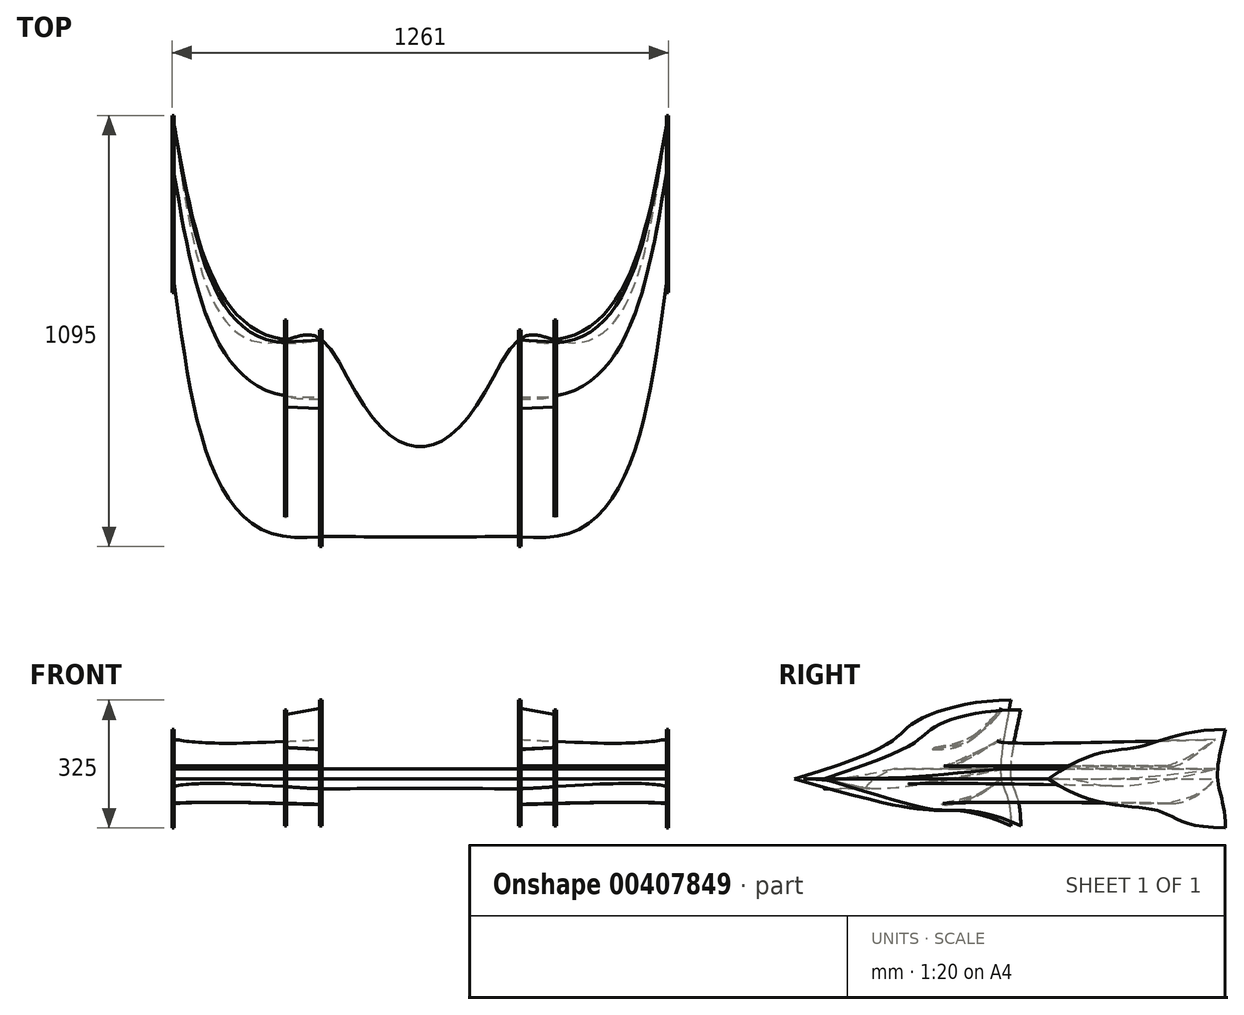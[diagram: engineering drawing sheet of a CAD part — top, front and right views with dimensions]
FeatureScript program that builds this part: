
annotation { "Feature Type Name" : "Feature", "Feature Type Description" : "" }
export const myFeature = defineFeature(function(context is Context, id is Id, definition is map)
    precondition{}
    {
        {
            var Q0;
            Q0=qCreatedBy(makeId("Right.planeOp"),FACE);
            cPlane(context, id + "F0", {"entities" : qUnion([Q0]), "cplaneType" : CPlaneType.OFFSET, "offset" : 250 * mm, "width" : 152.4 * mm, "height" : 152.4 * mm});
        }
        {
            var Q0;
            Q0=qCreatedBy(makeId("Right.planeOp"),FACE);
            cPlane(context, id + "F1", {"entities" : qUnion([Q0]), "cplaneType" : CPlaneType.OFFSET, "offset" : 340 * mm, "width" : 150 * mm, "height" : 150 * mm});
        }
        {
            var Q0;
            Q0=qCreatedBy(makeId("Right.planeOp"),FACE);
            cPlane(context, id + "F2", {"entities" : qUnion([Q0]), "cplaneType" : CPlaneType.OFFSET, "offset" : 625 * mm, "width" : 150 * mm, "height" : 150 * mm});
        }
        {
            var Q0;
            Q0=qCreatedBy(id+"F0.planeOp",FACE);
            var sketch = newSketch(context, id + "F3", { "sketchPlane" : qUnion([Q0])});
            skPoint(sketch, "E0.middle", {"position": v(0, 0) * mm});
            skFitSpline(sketch, "E1", {"points": [v(-275, 0) * mm, v(25, 140) * mm, v(275, 200) * mm], "startDerivative": vector(1552.03, 451.5) * mm, "endDerivative": vector(720.48, 0) * mm});
            skFitSpline(sketch, "E2", {"points": [v(275, 200) * mm, v(250, 0) * mm, v(275, -120) * mm], "startDerivative": vector(-73.02, -379.03) * mm, "endDerivative": vector(0, -547.76) * mm});
            skFitSpline(sketch, "E3", {"points": [v(-275, 0) * mm, v(100, -80) * mm, v(275, -120) * mm], "startDerivative": vector(1389.49, -404.21) * mm, "endDerivative": vector(646.14, -295.38) * mm});
            skSolve(sketch);
        }
        {
            var Q0;
            Q0=qCreatedBy(id+"F1.planeOp",FACE);
            var sketch = newSketch(context, id + "F4", { "sketchPlane" : qUnion([Q0])});
            skFitSpline(sketch, "E4", {"points": [v(-200, 0) * mm, v(75, 127.5) * mm, v(300, 175) * mm], "startDerivative": vector(1403.25, 449.04) * mm, "endDerivative": vector(773.32, 0) * mm});
            skFitSpline(sketch, "E5", {"points": [v(300, 175) * mm, v(275, 0) * mm, v(300, -120) * mm], "startDerivative": vector(-73.33, -336.17) * mm, "endDerivative": vector(0, -528.22) * mm});
            skFitSpline(sketch, "E6", {"points": [v(-200, 0) * mm, v(125, -80) * mm, v(300, -120) * mm], "startDerivative": vector(1299.26, -415.76) * mm, "endDerivative": vector(620.93, -283.86) * mm});
            skSolve(sketch);
        }
        {
            var Q0;
            Q0=qCreatedBy(id+"F2.planeOp",FACE);
            var sketch = newSketch(context, id + "F5", { "sketchPlane" : qUnion([Q0])});
            skFitSpline(sketch, "E7", {"points": [v(370, 0) * mm, v(595, 80) * mm, v(820, 125) * mm], "startDerivative": vector(668.33, 475.26) * mm, "endDerivative": vector(681.8, 0) * mm});
            skFitSpline(sketch, "E8", {"points": [v(820, 125) * mm, v(800, 0) * mm, v(820, -125) * mm], "startDerivative": vector(-60, -250) * mm, "endDerivative": vector(0, -375) * mm});
            skFitSpline(sketch, "E9", {"points": [v(370, 0) * mm, v(645, -80) * mm, v(820, -125) * mm], "startDerivative": vector(605.58, -430.63) * mm, "endDerivative": vector(762.4, 0) * mm});
            skSolve(sketch);
        }
        {
            var Q0;
            Q0=qCreatedBy(makeId("Right.planeOp"),FACE);
            cPlane(context, id + "F6", {"entities" : qUnion([Q0]), "cplaneType" : CPlaneType.OFFSET, "offset" : 160 * mm, "width" : 150 * mm, "height" : 150 * mm});
        }
        {
            var Q0;
            Q0=qCreatedBy(id+"F6.planeOp",FACE);
            var sketch = newSketch(context, id + "F7", { "sketchPlane" : qUnion([Q0])});
            skFitSpline(sketch, "E10", {"points": [v(-250, 0) * mm, v(-75, -25) * mm, v(110, 25) * mm], "startDerivative": vector(535.81, 0) * mm, "endDerivative": vector(529.32, 147.03) * mm});
            skFitSpline(sketch, "E11", {"points": [v(-250, 0) * mm, v(110, 25) * mm], "startDerivative": vector(540, 0) * mm, "endDerivative": vector(540, 75) * mm});
            skSolve(sketch);
        }
        {
            var Q0;
            Q0=qCreatedBy(makeId("Right.planeOp"),FACE);
            cPlane(context, id + "F8", {"entities" : qUnion([Q0]), "cplaneType" : CPlaneType.OFFSET, "offset" : 250 * mm, "width" : 150 * mm, "height" : 150 * mm});
        }
        {
            var Q0;
            Q0=qCreatedBy(id+"F8.planeOp",FACE);
            var sketch = newSketch(context, id + "F9", { "sketchPlane" : qUnion([Q0])});
            skFitSpline(sketch, "E12", {"points": [v(-250, 0) * mm, v(-75, -25) * mm, v(250, 25) * mm], "startDerivative": vector(620.51, 0) * mm, "endDerivative": vector(649.96, 130) * mm});
            skFitSpline(sketch, "E13", {"points": [v(-250, 0) * mm, v(250, 25) * mm], "startDerivative": vector(750, 0) * mm, "endDerivative": vector(750, 75) * mm});
            skSolve(sketch);
        }
        {
            var Q0;
            Q0=qCreatedBy(id+"F8.planeOp",FACE);
            var sketch = newSketch(context, id + "F10", { "sketchPlane" : qUnion([Q0])});
            skFitSpline(sketch, "E14", {"points": [v(105, 32) * mm, v(125, 32) * mm, v(250, 100) * mm], "startDerivative": vector(59.92, -12.75) * mm, "endDerivative": vector(207.69, 127.5) * mm});
            skFitSpline(sketch, "E15", {"points": [v(105, 32) * mm, v(250, 100) * mm], "startDerivative": vector(153.75, 54) * mm, "endDerivative": vector(281.25, 150) * mm});
            skSolve(sketch);
        }
        {
            var Q0;
            Q0=qCreatedBy(id+"F8.planeOp",FACE);
            var sketch = newSketch(context, id + "F11", { "sketchPlane" : qUnion([Q0])});
            skFitSpline(sketch, "E16", {"points": [v(100, -65) * mm, v(125, -65) * mm, v(250, 0) * mm], "startDerivative": vector(70.52, -13.7) * mm, "endDerivative": vector(266.48, 234.5) * mm});
            skFitSpline(sketch, "E17", {"points": [v(100, -65) * mm, v(250, 0) * mm], "startDerivative": vector(168.75, 60) * mm, "endDerivative": vector(187.5, 165) * mm});
            skSolve(sketch);
        }
        {
            var Q0;
            Q0=qCreatedBy(id+"F8.planeOp",FACE);
            var sketch = newSketch(context, id + "F12", { "sketchPlane" : qUnion([Q0])});
            skFitSpline(sketch, "E18", {"points": [v(75, 75) * mm, v(100, 75) * mm, v(250, 180) * mm], "startDerivative": vector(77.44, -19.4) * mm, "endDerivative": vector(308.14, 431.4) * mm});
            skFitSpline(sketch, "E19", {"points": [v(75, 75) * mm, v(250, 180) * mm], "startDerivative": vector(187.5, 37.5) * mm, "endDerivative": vector(225, 277.5) * mm});
            skSolve(sketch);
        }
        {
            var Q0;
            Q0=qCreatedBy(makeId("Right.planeOp"),FACE);
            cPlane(context, id + "F13", {"entities" : qUnion([Q0]), "cplaneType" : CPlaneType.OFFSET, "offset" : 340 * mm, "width" : 150 * mm, "height" : 150 * mm});
        }
        {
            var Q0;
            Q0=qCreatedBy(id+"F13.planeOp",FACE);
            var sketch = newSketch(context, id + "F14", { "sketchPlane" : qUnion([Q0])});
            skFitSpline(sketch, "E20", {"points": [v(-250, 0) * mm, v(-75, -20) * mm, v(250, 25) * mm], "startDerivative": vector(620.77, 0) * mm, "endDerivative": vector(649.76, 129.95) * mm});
            skFitSpline(sketch, "E21", {"points": [v(-250, 0) * mm, v(250, 25) * mm], "startDerivative": vector(750, 0) * mm, "endDerivative": vector(750, 75) * mm});
            skSolve(sketch);
        }
        {
            var Q0;
            Q0=qCreatedBy(id+"F13.planeOp",FACE);
            var sketch = newSketch(context, id + "F15", { "sketchPlane" : qUnion([Q0])});
            skFitSpline(sketch, "E22", {"points": [v(107.5, 32.5) * mm, v(125, 32.5) * mm, v(242, 95) * mm], "startDerivative": vector(53.18, -11.35) * mm, "endDerivative": vector(193.9, 116.45) * mm});
            skFitSpline(sketch, "E23", {"points": [v(107.5, 32.5) * mm, v(242, 95) * mm], "startDerivative": vector(140.25, 52.5) * mm, "endDerivative": vector(263.25, 135) * mm});
            skSolve(sketch);
        }
        {
            var Q0;
            Q0=qCreatedBy(id+"F13.planeOp",FACE);
            var sketch = newSketch(context, id + "F16", { "sketchPlane" : qUnion([Q0])});
            skFitSpline(sketch, "E24", {"points": [v(105, -62.5) * mm, v(125, -62.5) * mm, v(250, 0) * mm], "startDerivative": vector(59.23, -11.82) * mm, "endDerivative": vector(258.43, 222.25) * mm});
            skFitSpline(sketch, "E25", {"points": [v(105, -62.5) * mm, v(250, 0) * mm], "startDerivative": vector(153.75, 52.5) * mm, "endDerivative": vector(187.5, 161.25) * mm});
            skSolve(sketch);
        }
        {
            var Q0;
            Q0=qCreatedBy(id+"F13.planeOp",FACE);
            var sketch = newSketch(context, id + "F17", { "sketchPlane" : qUnion([Q0])});
            skFitSpline(sketch, "E26", {"points": [v(80, 80) * mm, v(100, 80) * mm, v(245, 164) * mm], "startDerivative": vector(62.85, -14.5) * mm, "endDerivative": vector(292.64, 339.06) * mm});
            skFitSpline(sketch, "E27", {"points": [v(80, 80) * mm, v(245, 164) * mm], "startDerivative": vector(168.75, 30) * mm, "endDerivative": vector(217.5, 222) * mm});
            skSolve(sketch);
        }
        {
            var Q0;
            Q0=qCreatedBy(makeId("Right.planeOp"),FACE);
            cPlane(context, id + "F18", {"entities" : qUnion([Q0]), "cplaneType" : CPlaneType.OFFSET, "offset" : 625 * mm, "width" : 150 * mm, "height" : 150 * mm});
        }
        {
            var Q0;
            Q0=qCreatedBy(id+"F18.planeOp",FACE);
            var sketch = newSketch(context, id + "F19", { "sketchPlane" : qUnion([Q0])});
            skFitSpline(sketch, "E28", {"points": [v(395, 0) * mm, v(520, -18) * mm, v(795, 25) * mm], "startDerivative": vector(465.86, 0) * mm, "endDerivative": vector(502.08, 125.52) * mm});
            skFitSpline(sketch, "E29", {"points": [v(395, 0) * mm, v(795, 25) * mm], "startDerivative": vector(600, 0) * mm, "endDerivative": vector(600, 75) * mm});
            skSolve(sketch);
        }
        {
            var Q0;
            Q0=qCreatedBy(id+"F18.planeOp",FACE);
            var sketch = newSketch(context, id + "F20", { "sketchPlane" : qUnion([Q0])});
            skFitSpline(sketch, "E30", {"points": [v(670, 33) * mm, v(695, 33) * mm, v(795, 100) * mm], "startDerivative": vector(69.57, -15.27) * mm, "endDerivative": vector(168.14, 131.03) * mm});
            skFitSpline(sketch, "E31", {"points": [v(670, 33) * mm, v(795, 100) * mm], "startDerivative": vector(150, 51) * mm, "endDerivative": vector(225, 150) * mm});
            skSolve(sketch);
        }
        {
            var Q0;
            Q0=qCreatedBy(id+"F18.planeOp",FACE);
            var sketch = newSketch(context, id + "F21", { "sketchPlane" : qUnion([Q0])});
            skFitSpline(sketch, "E32", {"points": [v(677, -62) * mm, v(695, -62) * mm, v(795, 0) * mm], "startDerivative": vector(53.46, -12.13) * mm, "endDerivative": vector(208.67, 223.28) * mm});
            skFitSpline(sketch, "E33", {"points": [v(677, -62) * mm, v(795, 0) * mm], "startDerivative": vector(129, 51) * mm, "endDerivative": vector(150, 160.5) * mm});
            skSolve(sketch);
        }
        {
            var Q0;
            Q0=qCreatedBy(makeId("Right.planeOp"),FACE);
            cPlane(context, id + "F22", {"entities" : qUnion([Q0]), "cplaneType" : CPlaneType.OFFSET, "offset" : 250 * mm, "oppositeDirection" : true, "width" : 150 * mm, "height" : 150 * mm});
        }
        {
            var Q0;
            Q0=qCreatedBy(makeId("Right.planeOp"),FACE);
            cPlane(context, id + "F23", {"entities" : qUnion([Q0]), "cplaneType" : CPlaneType.OFFSET, "offset" : 340 * mm, "oppositeDirection" : true, "width" : 150 * mm, "height" : 150 * mm});
        }
        {
            var Q0;
            Q0=qCreatedBy(makeId("Right.planeOp"),FACE);
            cPlane(context, id + "F24", {"entities" : qUnion([Q0]), "cplaneType" : CPlaneType.OFFSET, "offset" : 625 * mm, "oppositeDirection" : true, "width" : 150 * mm, "height" : 150 * mm});
        }
        {
            var Q0;
            Q0=qCreatedBy(id+"F22.planeOp",FACE);
            var sketch = newSketch(context, id + "F25", { "sketchPlane" : qUnion([Q0])});
            skPoint(sketch, "E34.middle", {"position": v(0, 0) * mm});
            skFitSpline(sketch, "E35", {"points": [v(-275, 0) * mm, v(25, 140) * mm, v(275, 200) * mm], "startDerivative": vector(1552.03, 451.5) * mm, "endDerivative": vector(720.48, 0) * mm});
            skFitSpline(sketch, "E36", {"points": [v(275, 200) * mm, v(250, 0) * mm, v(275, -120) * mm], "startDerivative": vector(-73.02, -379.03) * mm, "endDerivative": vector(0, -547.76) * mm});
            skFitSpline(sketch, "E37", {"points": [v(-275, 0) * mm, v(100, -80) * mm, v(275, -120) * mm], "startDerivative": vector(1389.49, -404.21) * mm, "endDerivative": vector(646.14, -295.38) * mm});
            skSolve(sketch);
        }
        {
            var Q0;
            Q0=qCreatedBy(id+"F23.planeOp",FACE);
            var sketch = newSketch(context, id + "F26", { "sketchPlane" : qUnion([Q0])});
            skFitSpline(sketch, "E38", {"points": [v(-200, 0) * mm, v(75, 127.5) * mm, v(300, 175) * mm], "startDerivative": vector(1403.25, 449.04) * mm, "endDerivative": vector(773.32, 0) * mm});
            skFitSpline(sketch, "E39", {"points": [v(300, 175) * mm, v(275, 0) * mm, v(300, -120) * mm], "startDerivative": vector(-73.33, -336.17) * mm, "endDerivative": vector(0, -528.22) * mm});
            skFitSpline(sketch, "E40", {"points": [v(-200, 0) * mm, v(125, -80) * mm, v(300, -120) * mm], "startDerivative": vector(1299.26, -415.76) * mm, "endDerivative": vector(620.93, -283.86) * mm});
            skSolve(sketch);
        }
        {
            var Q0;
            Q0=qCreatedBy(id+"F24.planeOp",FACE);
            var sketch = newSketch(context, id + "F27", { "sketchPlane" : qUnion([Q0])});
            skLineSegment(sketch, "E41", {"start": v(820, -80) * mm, "end": v(820, -125) * mm});
            skFitSpline(sketch, "E42", {"points": [v(370, 0) * mm, v(595, 80) * mm, v(820, 125) * mm], "startDerivative": vector(668.33, 475.26) * mm, "endDerivative": vector(681.8, 0) * mm});
            skFitSpline(sketch, "E43", {"points": [v(820, 125) * mm, v(800, 0) * mm, v(820, -125) * mm], "startDerivative": vector(-60, -250) * mm, "endDerivative": vector(0, -375) * mm});
            skFitSpline(sketch, "E44", {"points": [v(370, 0) * mm, v(645, -80) * mm, v(820, -125) * mm], "startDerivative": vector(605.58, -430.63) * mm, "endDerivative": vector(762.4, 0) * mm});
            skSolve(sketch);
        }
        {
            var Q0;
            Q0=qCreatedBy(makeId("Right.planeOp"),FACE);
            cPlane(context, id + "F28", {"entities" : qUnion([Q0]), "cplaneType" : CPlaneType.OFFSET, "offset" : 160 * mm, "oppositeDirection" : true, "width" : 150 * mm, "height" : 150 * mm});
        }
        {
            var Q0;
            Q0=qCreatedBy(id+"F28.planeOp",FACE);
            var sketch = newSketch(context, id + "F29", { "sketchPlane" : qUnion([Q0])});
            skFitSpline(sketch, "E45", {"points": [v(-250, 0) * mm, v(-75, -25) * mm, v(110, 25) * mm], "startDerivative": vector(535.81, 0) * mm, "endDerivative": vector(529.32, 147.03) * mm});
            skFitSpline(sketch, "E46", {"points": [v(-250, 0) * mm, v(110, 25) * mm], "startDerivative": vector(540, 0) * mm, "endDerivative": vector(540, 75) * mm});
            skSolve(sketch);
        }
        {
            var Q0;
            Q0=qCreatedBy(makeId("Right.planeOp"),FACE);
            cPlane(context, id + "F30", {"entities" : qUnion([Q0]), "cplaneType" : CPlaneType.OFFSET, "offset" : 250 * mm, "oppositeDirection" : true, "width" : 150 * mm, "height" : 150 * mm});
        }
        {
            var Q0;
            Q0=qCreatedBy(id+"F30.planeOp",FACE);
            var sketch = newSketch(context, id + "F31", { "sketchPlane" : qUnion([Q0])});
            skFitSpline(sketch, "E47", {"points": [v(-250, 0) * mm, v(-75, -25) * mm, v(250, 25) * mm], "startDerivative": vector(620.51, 0) * mm, "endDerivative": vector(606.46, 128.7) * mm});
            skFitSpline(sketch, "E48", {"points": [v(-250, 0) * mm, v(250, 25) * mm], "startDerivative": vector(750, 0) * mm, "endDerivative": vector(750, 75) * mm});
            skSolve(sketch);
        }
        {
            var Q0;
            Q0=qCreatedBy(id+"F30.planeOp",FACE);
            var sketch = newSketch(context, id + "F32", { "sketchPlane" : qUnion([Q0])});
            skFitSpline(sketch, "E49", {"points": [v(105, 32) * mm, v(125, 32) * mm, v(250, 100) * mm], "startDerivative": vector(59.92, -12.75) * mm, "endDerivative": vector(207.69, 127.5) * mm});
            skFitSpline(sketch, "E50", {"points": [v(105, 32) * mm, v(250, 100) * mm], "startDerivative": vector(153.75, 54) * mm, "endDerivative": vector(281.25, 150) * mm});
            skSolve(sketch);
        }
        {
            var Q0;
            Q0=qCreatedBy(id+"F30.planeOp",FACE);
            var sketch = newSketch(context, id + "F33", { "sketchPlane" : qUnion([Q0])});
            skFitSpline(sketch, "E51", {"points": [v(100, -65) * mm, v(125, -65) * mm, v(250, 0) * mm], "startDerivative": vector(70.52, -13.7) * mm, "endDerivative": vector(266.48, 234.5) * mm});
            skFitSpline(sketch, "E52", {"points": [v(100, -65) * mm, v(250, 0) * mm], "startDerivative": vector(168.75, 60) * mm, "endDerivative": vector(187.5, 165) * mm});
            skSolve(sketch);
        }
        {
            var Q0;
            Q0=qCreatedBy(id+"F30.planeOp",FACE);
            var sketch = newSketch(context, id + "F34", { "sketchPlane" : qUnion([Q0])});
            skFitSpline(sketch, "E53", {"points": [v(75, 75) * mm, v(100, 75) * mm, v(250, 180) * mm], "startDerivative": vector(77.44, -19.4) * mm, "endDerivative": vector(308.14, 431.4) * mm});
            skFitSpline(sketch, "E54", {"points": [v(75, 75) * mm, v(250, 180) * mm], "startDerivative": vector(187.5, 37.5) * mm, "endDerivative": vector(225, 277.5) * mm});
            skSolve(sketch);
        }
        {
            var Q0;
            Q0=qCreatedBy(makeId("Right.planeOp"),FACE);
            cPlane(context, id + "F35", {"entities" : qUnion([Q0]), "cplaneType" : CPlaneType.OFFSET, "offset" : 340 * mm, "oppositeDirection" : true, "width" : 150 * mm, "height" : 150 * mm});
        }
        {
            var Q0;
            Q0=qCreatedBy(id+"F35.planeOp",FACE);
            var sketch = newSketch(context, id + "F36", { "sketchPlane" : qUnion([Q0])});
            skFitSpline(sketch, "E55", {"points": [v(-250, 0) * mm, v(-75, -20) * mm, v(250, 25) * mm], "startDerivative": vector(620.77, 0) * mm, "endDerivative": vector(649.76, 129.95) * mm});
            skFitSpline(sketch, "E56", {"points": [v(-250, 0) * mm, v(250, 25) * mm], "startDerivative": vector(750, 0) * mm, "endDerivative": vector(750, 75) * mm});
            skSolve(sketch);
        }
        {
            var Q0;
            Q0=qCreatedBy(id+"F35.planeOp",FACE);
            var sketch = newSketch(context, id + "F37", { "sketchPlane" : qUnion([Q0])});
            skFitSpline(sketch, "E57", {"points": [v(107.5, 32.5) * mm, v(125, 32.5) * mm, v(242, 95) * mm], "startDerivative": vector(53.18, -11.35) * mm, "endDerivative": vector(193.9, 116.45) * mm});
            skFitSpline(sketch, "E58", {"points": [v(107.5, 32.5) * mm, v(242, 95) * mm], "startDerivative": vector(140.25, 52.5) * mm, "endDerivative": vector(263.25, 135) * mm});
            skSolve(sketch);
        }
        {
            var Q0;
            Q0=qCreatedBy(id+"F35.planeOp",FACE);
            var sketch = newSketch(context, id + "F38", { "sketchPlane" : qUnion([Q0])});
            skFitSpline(sketch, "E59", {"points": [v(105, -62.5) * mm, v(125, -62.5) * mm, v(250, 0) * mm], "startDerivative": vector(59.23, -11.82) * mm, "endDerivative": vector(258.43, 222.25) * mm});
            skFitSpline(sketch, "E60", {"points": [v(105, -62.5) * mm, v(250, 0) * mm], "startDerivative": vector(153.75, 52.5) * mm, "endDerivative": vector(187.5, 161.25) * mm});
            skSolve(sketch);
        }
        {
            var Q0;
            Q0=qCreatedBy(id+"F35.planeOp",FACE);
            var sketch = newSketch(context, id + "F39", { "sketchPlane" : qUnion([Q0])});
            skFitSpline(sketch, "E61", {"points": [v(80, 80) * mm, v(100, 80) * mm, v(245, 164) * mm], "startDerivative": vector(62.85, -14.5) * mm, "endDerivative": vector(292.64, 339.06) * mm});
            skFitSpline(sketch, "E62", {"points": [v(80, 80) * mm, v(245, 164) * mm], "startDerivative": vector(168.75, 30) * mm, "endDerivative": vector(217.5, 222) * mm});
            skSolve(sketch);
        }
        {
            var Q0;
            Q0=qCreatedBy(makeId("Right.planeOp"),FACE);
            cPlane(context, id + "F40", {"entities" : qUnion([Q0]), "cplaneType" : CPlaneType.OFFSET, "offset" : 625 * mm, "oppositeDirection" : true, "width" : 150 * mm, "height" : 150 * mm});
        }
        {
            var Q0;
            Q0=qCreatedBy(id+"F40.planeOp",FACE);
            var sketch = newSketch(context, id + "F41", { "sketchPlane" : qUnion([Q0])});
            skFitSpline(sketch, "E63", {"points": [v(395, 0) * mm, v(520, -18) * mm, v(795, 25) * mm], "startDerivative": vector(465.86, 0) * mm, "endDerivative": vector(502.08, 125.52) * mm});
            skFitSpline(sketch, "E64", {"points": [v(395, 0) * mm, v(795, 25) * mm], "startDerivative": vector(600, 0) * mm, "endDerivative": vector(600, 75) * mm});
            skSolve(sketch);
        }
        {
            var Q0;
            Q0=qCreatedBy(id+"F40.planeOp",FACE);
            var sketch = newSketch(context, id + "F42", { "sketchPlane" : qUnion([Q0])});
            skFitSpline(sketch, "E65", {"points": [v(670, 33) * mm, v(695, 33) * mm, v(795, 100) * mm], "startDerivative": vector(69.57, -15.27) * mm, "endDerivative": vector(168.14, 131.03) * mm});
            skFitSpline(sketch, "E66", {"points": [v(670, 33) * mm, v(795, 100) * mm], "startDerivative": vector(150, 51) * mm, "endDerivative": vector(225, 150) * mm});
            skSolve(sketch);
        }
        {
            var Q0;
            Q0=qCreatedBy(id+"F40.planeOp",FACE);
            var sketch = newSketch(context, id + "F43", { "sketchPlane" : qUnion([Q0])});
            skFitSpline(sketch, "E67", {"points": [v(677, -62) * mm, v(695, -62) * mm, v(795, 0) * mm], "startDerivative": vector(53.46, -12.13) * mm, "endDerivative": vector(208.67, 223.28) * mm});
            skFitSpline(sketch, "E68", {"points": [v(677, -62) * mm, v(795, 0) * mm], "startDerivative": vector(129, 51) * mm, "endDerivative": vector(150, 160.5) * mm});
            skSolve(sketch);
        }
        {
            var Q0;
            {var subQ0=sQuery(id+"F41.wireOp",EDGE,"E63");Q0=makeQuery(id+"F41.imprint","IMPRINT",FACE,{"disambiguationData":[TD([[makeQuery(id+"F41.imprint","IMPRINT",EDGE,{"derivedFrom":subQ0}),1.0]])]});}
            var Q1;
            {var subQ0=sQuery(id+"F36.wireOp",EDGE,"E55");Q1=makeQuery(id+"F36.imprint","IMPRINT",FACE,{"disambiguationData":[TD([[makeQuery(id+"F36.imprint","IMPRINT",EDGE,{"derivedFrom":subQ0}),1.0]])]});}
            var Q2;
            {var subQ0=sQuery(id+"F31.wireOp",EDGE,"E47");Q2=makeQuery(id+"F31.imprint","IMPRINT",FACE,{"disambiguationData":[TD([[makeQuery(id+"F31.imprint","IMPRINT",EDGE,{"derivedFrom":subQ0}),1.0]])]});}
            var Q3;
            {var subQ0=sQuery(id+"F29.wireOp",EDGE,"E45");Q3=makeQuery(id+"F29.imprint","IMPRINT",FACE,{"disambiguationData":[TD([[makeQuery(id+"F29.imprint","IMPRINT",EDGE,{"derivedFrom":subQ0}),1.0]])]});}
            var Q4;
            {var subQ0=sQuery(id+"F7.wireOp",EDGE,"E10");Q4=makeQuery(id+"F7.imprint","IMPRINT",FACE,{"disambiguationData":[TD([[makeQuery(id+"F7.imprint","IMPRINT",EDGE,{"derivedFrom":subQ0}),1.0]])]});}
            var Q5;
            {var subQ0=sQuery(id+"F9.wireOp",EDGE,"E12");Q5=makeQuery(id+"F9.imprint","IMPRINT",FACE,{"disambiguationData":[TD([[makeQuery(id+"F9.imprint","IMPRINT",EDGE,{"derivedFrom":subQ0}),1.0]])]});}
            var Q6;
            {var subQ0=sQuery(id+"F14.wireOp",EDGE,"E20");Q6=makeQuery(id+"F14.imprint","IMPRINT",FACE,{"disambiguationData":[TD([[makeQuery(id+"F14.imprint","IMPRINT",EDGE,{"derivedFrom":subQ0}),1.0]])]});}
            var Q7;
            {var subQ0=sQuery(id+"F19.wireOp",EDGE,"E28");Q7=makeQuery(id+"F19.imprint","IMPRINT",FACE,{"disambiguationData":[TD([[makeQuery(id+"F19.imprint","IMPRINT",EDGE,{"derivedFrom":subQ0}),1.0]])]});}
            loft(context, id + "F44", {"sheetProfilesArray" : [{ "sheetProfileEntities" : qUnion([Q0]) }, { "sheetProfileEntities" : qUnion([Q1]) }, { "sheetProfileEntities" : qUnion([Q2]) }, { "sheetProfileEntities" : qUnion([Q3]) }, { "sheetProfileEntities" : qUnion([Q4]) }, { "sheetProfileEntities" : qUnion([Q5]) }, { "sheetProfileEntities" : qUnion([Q6]) }, { "sheetProfileEntities" : qUnion([Q7]) }]});
        }
        {
            var Q0;
            Q0=makeQuery(id+"F42.imprint","IMPRINT",FACE,{"disambiguationData":[TD([[makeQuery(id+"F42.imprint","IMPRINT",EDGE,{"derivedFrom":sQuery(id+"F42.wireOp",EDGE,"E65")}),1.0]])]});
            var Q1;
            Q1=makeQuery(id+"F37.imprint","IMPRINT",FACE,{"disambiguationData":[TD([[makeQuery(id+"F37.imprint","IMPRINT",EDGE,{"derivedFrom":sQuery(id+"F37.wireOp",EDGE,"E57")}),1.0]])]});
            var Q2;
            Q2=makeQuery(id+"F32.imprint","IMPRINT",FACE,{"disambiguationData":[TD([[makeQuery(id+"F32.imprint","IMPRINT",EDGE,{"derivedFrom":sQuery(id+"F32.wireOp",EDGE,"E49")}),1.0]])]});
            loft(context, id + "F45", {"sheetProfilesArray" : [{ "sheetProfileEntities" : qUnion([Q0]) }, { "sheetProfileEntities" : qUnion([Q1]) }, { "sheetProfileEntities" : qUnion([Q2]) }]});
        }
        {
            var Q0;
            Q0=makeQuery(id+"F10.imprint","IMPRINT",FACE,{"disambiguationData":[TD([[makeQuery(id+"F10.imprint","IMPRINT",EDGE,{"derivedFrom":sQuery(id+"F10.wireOp",EDGE,"E14")}),1.0]])]});
            var Q1;
            Q1=makeQuery(id+"F15.imprint","IMPRINT",FACE,{"disambiguationData":[TD([[makeQuery(id+"F15.imprint","IMPRINT",EDGE,{"derivedFrom":sQuery(id+"F15.wireOp",EDGE,"E22")}),1.0]])]});
            var Q2;
            Q2=makeQuery(id+"F20.imprint","IMPRINT",FACE,{"disambiguationData":[TD([[makeQuery(id+"F20.imprint","IMPRINT",EDGE,{"derivedFrom":sQuery(id+"F20.wireOp",EDGE,"E30")}),1.0]])]});
            loft(context, id + "F46", {"sheetProfilesArray" : [{ "sheetProfileEntities" : qUnion([Q0]) }, { "sheetProfileEntities" : qUnion([Q1]) }, { "sheetProfileEntities" : qUnion([Q2]) }]});
        }
        {
            var Q0;
            {var subQ0=sQuery(id+"F43.wireOp",EDGE,"E67");Q0=makeQuery(id+"F43.imprint","IMPRINT",FACE,{"disambiguationData":[TD([[makeQuery(id+"F43.imprint","IMPRINT",EDGE,{"derivedFrom":subQ0}),1.0]])]});}
            var Q1;
            {var subQ0=sQuery(id+"F38.wireOp",EDGE,"E59");Q1=makeQuery(id+"F38.imprint","IMPRINT",FACE,{"disambiguationData":[TD([[makeQuery(id+"F38.imprint","IMPRINT",EDGE,{"derivedFrom":subQ0}),1.0]])]});}
            var Q2;
            {var subQ0=sQuery(id+"F33.wireOp",EDGE,"E51");Q2=makeQuery(id+"F33.imprint","IMPRINT",FACE,{"disambiguationData":[TD([[makeQuery(id+"F33.imprint","IMPRINT",EDGE,{"derivedFrom":subQ0}),1.0]])]});}
            loft(context, id + "F47", {"sheetProfilesArray" : [{ "sheetProfileEntities" : qUnion([Q0]) }, { "sheetProfileEntities" : qUnion([Q1]) }, { "sheetProfileEntities" : qUnion([Q2]) }]});
        }
        {
            var Q0;
            {var subQ0=sQuery(id+"F11.wireOp",EDGE,"E16");Q0=makeQuery(id+"F11.imprint","IMPRINT",FACE,{"disambiguationData":[TD([[makeQuery(id+"F11.imprint","IMPRINT",EDGE,{"derivedFrom":subQ0}),1.0]])]});}
            var Q1;
            {var subQ0=sQuery(id+"F16.wireOp",EDGE,"E24");Q1=makeQuery(id+"F16.imprint","IMPRINT",FACE,{"disambiguationData":[TD([[makeQuery(id+"F16.imprint","IMPRINT",EDGE,{"derivedFrom":subQ0}),1.0]])]});}
            var Q2;
            {var subQ0=sQuery(id+"F21.wireOp",EDGE,"E32");Q2=makeQuery(id+"F21.imprint","IMPRINT",FACE,{"disambiguationData":[TD([[makeQuery(id+"F21.imprint","IMPRINT",EDGE,{"derivedFrom":subQ0}),1.0]])]});}
            loft(context, id + "F48", {"sheetProfilesArray" : [{ "sheetProfileEntities" : qUnion([Q0]) }, { "sheetProfileEntities" : qUnion([Q1]) }, { "sheetProfileEntities" : qUnion([Q2]) }]});
        }
        {
            var Q0;
            Q0=makeQuery(id+"F34.imprint","IMPRINT",FACE,{"disambiguationData":[TD([[makeQuery(id+"F34.imprint","IMPRINT",EDGE,{"derivedFrom":sQuery(id+"F34.wireOp",EDGE,"E53")}),1.0]])]});
            var Q1;
            Q1=makeQuery(id+"F39.imprint","IMPRINT",FACE,{"disambiguationData":[TD([[makeQuery(id+"F39.imprint","IMPRINT",EDGE,{"derivedFrom":sQuery(id+"F39.wireOp",EDGE,"E61")}),1.0]])]});
            loft(context, id + "F49", {"sheetProfilesArray" : [{ "sheetProfileEntities" : qUnion([Q0]) }, { "sheetProfileEntities" : qUnion([Q1]) }]});
        }
        {
            var Q0;
            Q0=makeQuery(id+"F12.imprint","IMPRINT",FACE,{"disambiguationData":[TD([[makeQuery(id+"F12.imprint","IMPRINT",EDGE,{"derivedFrom":sQuery(id+"F12.wireOp",EDGE,"E18")}),1.0]])]});
            var Q1;
            Q1=makeQuery(id+"F17.imprint","IMPRINT",FACE,{"disambiguationData":[TD([[makeQuery(id+"F17.imprint","IMPRINT",EDGE,{"derivedFrom":sQuery(id+"F17.wireOp",EDGE,"E26")}),1.0]])]});
            loft(context, id + "F50", {"sheetProfilesArray" : [{ "sheetProfileEntities" : qUnion([Q0]) }, { "sheetProfileEntities" : qUnion([Q1]) }]});
        }
        {
            var Q0;
            Q0=makeQuery(id+"F25.imprint","IMPRINT",FACE,{"disambiguationData":[TD([[makeQuery(id+"F25.imprint","IMPRINT",EDGE,{"derivedFrom":sQuery(id+"F25.wireOp",EDGE,"E35")}),-1.0]])]});
            extrude(context, id + "F51", {"entities" : qUnion([Q0]), "oppositeDirection" : true, "depth" : 5.5 * mm});
        }
        {
            var Q0;
            Q0=makeQuery(id+"F3.imprint","IMPRINT",FACE,{"disambiguationData":[TD([[makeQuery(id+"F3.imprint","IMPRINT",EDGE,{"derivedFrom":sQuery(id+"F3.wireOp",EDGE,"E1")}),-1.0]])]});
            extrude(context, id + "F52", {"entities" : qUnion([Q0]), "depth" : 5.5 * mm});
        }
        {
            var Q0;
            Q0=makeQuery(id+"F26.imprint","IMPRINT",FACE,{"disambiguationData":[TD([[makeQuery(id+"F26.imprint","IMPRINT",EDGE,{"derivedFrom":sQuery(id+"F26.wireOp",EDGE,"E38")}),-1.0]])]});
            extrude(context, id + "F53", {"entities" : qUnion([Q0]), "oppositeDirection" : true, "depth" : 5.5 * mm});
        }
        {
            var Q0;
            Q0=makeQuery(id+"F4.imprint","IMPRINT",FACE,{"disambiguationData":[TD([[makeQuery(id+"F4.imprint","IMPRINT",EDGE,{"derivedFrom":sQuery(id+"F4.wireOp",EDGE,"E4")}),-1.0]])]});
            extrude(context, id + "F54", {"entities" : qUnion([Q0]), "depth" : 5.5 * mm});
        }
        {
            var Q0;
            Q0=makeQuery(id+"F27.imprint","IMPRINT",FACE,{"disambiguationData":[TD([[makeQuery(id+"F27.imprint","IMPRINT",EDGE,{"derivedFrom":sQuery(id+"F27.wireOp",EDGE,"E42")}),-1.0]])]});
            extrude(context, id + "F55", {"entities" : qUnion([Q0]), "oppositeDirection" : true, "depth" : 5.5 * mm});
        }
        {
            var Q0;
            Q0=makeQuery(id+"F5.imprint","IMPRINT",FACE,{"disambiguationData":[TD([[makeQuery(id+"F5.imprint","IMPRINT",EDGE,{"derivedFrom":sQuery(id+"F5.wireOp",EDGE,"E7")}),-1.0]])]});
            extrude(context, id + "F56", {"entities" : qUnion([Q0]), "depth" : 5.5 * mm});
        }
    });
